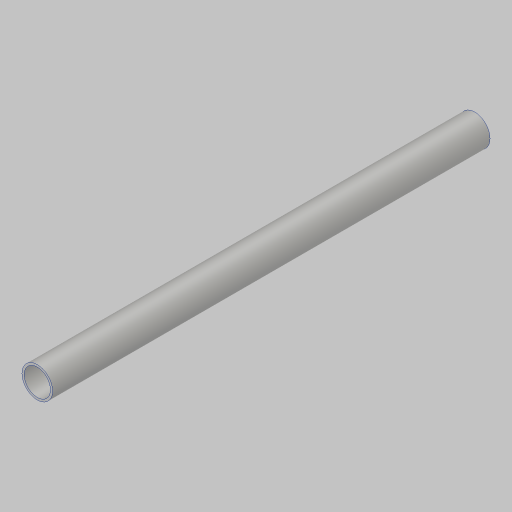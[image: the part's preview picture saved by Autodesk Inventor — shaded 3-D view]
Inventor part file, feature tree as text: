
AUTODESK INVENTOR PART (.ipt)
format: ipt  version: 2023.5 (Build 275446000, 446)  size: 88,576 bytes
history: native  units: in
note: dims shown in document units (in); Inventor stores cm internally (conversion verified against a paired STEP export)
features: extrude x1, sketch x1
ambient origin geometry x8: Origin, YZ Plane, XZ Plane, XY Plane, X Axis, Y Axis, Z Axis, Center Point
bodies: Solid1 (feature_tree)
feature tree (2):
  extrude  "Extrusion1"  Depth=12.5in
  sketch  "Sketch1"  dims[d0=0.875in d1=0.0625in d2=12.5in d3=0.0in]
